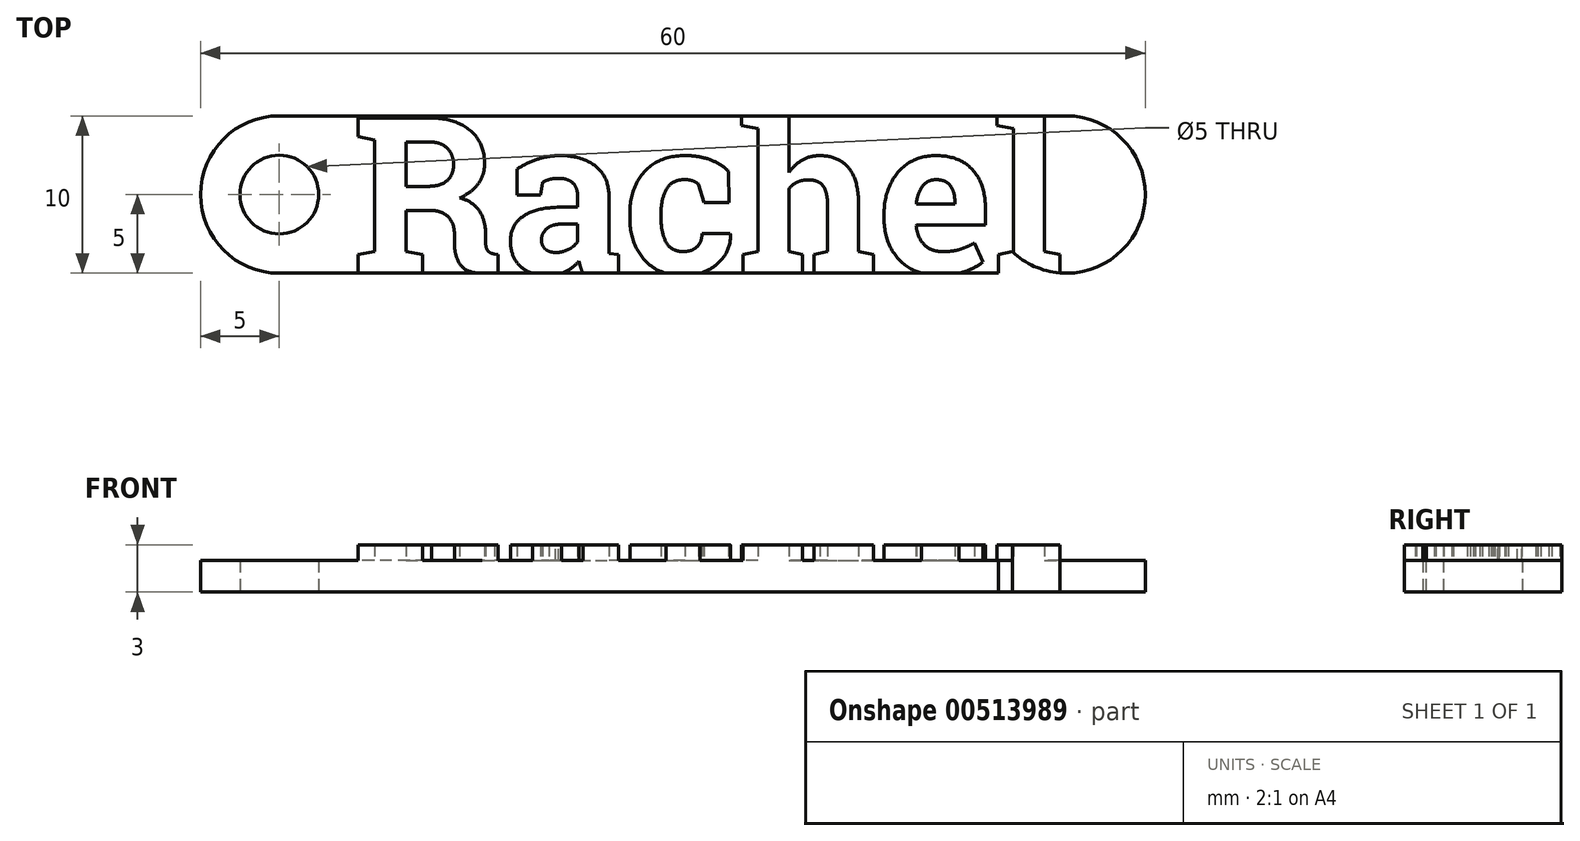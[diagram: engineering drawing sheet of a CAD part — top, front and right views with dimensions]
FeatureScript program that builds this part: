
annotation { "Feature Type Name" : "Feature", "Feature Type Description" : "" }
export const myFeature = defineFeature(function(context is Context, id is Id, definition is map)
    precondition{}
    {
        {
            var Q0;
            Q0=qCreatedBy(makeId("Top.planeOp"),FACE);
            var sketch = newSketch(context, id + "F0", { "sketchPlane" : qUnion([Q0])});
            skCircle(sketch, "E0", {"center": v(-30, 0) * mm, "radius": 2.5 * mm});
            skCircle(sketch, "E1", {"center": v(-30, 0) * mm, "radius": 5 * mm});
            skCircle(sketch, "E2", {"center": v(20, 0) * mm, "radius": 5 * mm});
            skLineSegment(sketch, "E3", {"start": v(-30, 5) * mm, "end": v(20, 5) * mm});
            skLineSegment(sketch, "E4", {"start": v(-30, -5) * mm, "end": v(20, -5) * mm});
            skText(sketch, "E5", { "text": "Rachel", "fontName": "RobotoSlab-Bold.ttf"});
            const initialGuessF0  = {"E5": [-0.02537, -0.005, 1, 0, 0.01]};
            skSetInitialGuess(sketch, initialGuessF0);
            skSolve(sketch);
        }
        {
            var Q0;
            {var subQ0=sQuery(id+"F0.wireOp",EDGE,"6bbc4e0a-0422-471a-a432-42bab2623723.sketch_text.stroke-9");Q0=makeQuery(id+"F0.imprint","IMPRINT",FACE,{"disambiguationData":[TD([[makeQuery(id+"F0.imprint","IMPRINT",EDGE,{"derivedFrom":subQ0}),1.0]])]});}
            var Q1;
            Q1=makeQuery(id+"F0.imprint","IMPRINT",FACE,{"disambiguationData":[TD([[makeQuery(id+"F0.imprint","IMPRINT",EDGE,{"derivedFrom":sQuery(id+"F0.wireOp",EDGE,"6bbc4e0a-0422-471a-a432-42bab2623723.sketch_text.stroke-0")}),1.0]])]});
            var Q2;
            Q2=makeQuery(id+"F0.imprint","IMPRINT",FACE,{"disambiguationData":[TD([[makeQuery(id+"F0.imprint","IMPRINT",EDGE,{"derivedFrom":sQuery(id+"F0.wireOp",EDGE,"6bbc4e0a-0422-471a-a432-42bab2623723.sketch_text.stroke-55")}),1.0]])]});
            var Q3;
            {var subQ5=sQuery(id+"F0.wireOp",EDGE,"6bbc4e0a-0422-471a-a432-42bab2623723.sketch_text.stroke-47");Q3=makeQuery(id+"F0.imprint","IMPRINT",FACE,{"disambiguationData":[TD([[makeQuery(id+"F0.imprint","IMPRINT",EDGE,{"derivedFrom":subQ5}),1.0]])]});}
            var Q4;
            {var subQ0=sQuery(id+"F0.wireOp",EDGE,"6bbc4e0a-0422-471a-a432-42bab2623723.sketch_text.stroke-71");Q4=makeQuery(id+"F0.imprint","IMPRINT",FACE,{"disambiguationData":[TD([[makeQuery(id+"F0.imprint","IMPRINT",EDGE,{"derivedFrom":subQ0}),1.0]])]});}
            var Q5;
            {var subQ0=sQuery(id+"F0.wireOp",EDGE,"E2");var subQ1=makeQuery(id+"F0.imprint","INTERSECT",VERTEX,{"derivedFrom":[subQ0,sQuery(id+"F0.wireOp",EDGE,"E3")]});Q5=makeQuery(id+"F0.imprint","IMPRINT",FACE,{"disambiguationData":[TD([[makeQuery(id+"F0.imprint","IMPRINT",EDGE,{"disambiguationData":[TD([[subQ1,-1.0]])],"derivedFrom":subQ0}),1.0]])]});}
            var Q6;
            Q6=makeQuery(id+"F0.imprint","IMPRINT",FACE,{"disambiguationData":[TD([[makeQuery(id+"F0.imprint","IMPRINT",EDGE,{"derivedFrom":sQuery(id+"F0.wireOp",EDGE,"E0")}),-1.0]])]});
            var Q7;
            Q7=makeQuery(id+"F0.imprint","IMPRINT",FACE,{"disambiguationData":[TD([[makeQuery(id+"F0.imprint","IMPRINT",EDGE,{"derivedFrom":sQuery(id+"F0.wireOp",EDGE,"6bbc4e0a-0422-471a-a432-42bab2623723.sketch_text.stroke-0")}),-1.0]])]});
            var Q8;
            Q8=makeQuery(id+"F0.imprint","IMPRINT",FACE,{"disambiguationData":[TD([[makeQuery(id+"F0.imprint","IMPRINT",EDGE,{"derivedFrom":sQuery(id+"F0.wireOp",EDGE,"6bbc4e0a-0422-471a-a432-42bab2623723.sketch_text.stroke-28")}),-1.0]])]});
            var Q9;
            {var subQ13=sQuery(id+"F0.wireOp",EDGE,"6bbc4e0a-0422-471a-a432-42bab2623723.sketch_text.stroke-47");Q9=makeQuery(id+"F0.imprint","IMPRINT",FACE,{"disambiguationData":[TD([[makeQuery(id+"F0.imprint","IMPRINT",EDGE,{"derivedFrom":subQ13}),-1.0]])]});}
            var Q10;
            Q10=makeQuery(id+"F0.imprint","IMPRINT",FACE,{"disambiguationData":[TD([[makeQuery(id+"F0.imprint","IMPRINT",EDGE,{"derivedFrom":sQuery(id+"F0.wireOp",EDGE,"6bbc4e0a-0422-471a-a432-42bab2623723.sketch_text.stroke-63")}),-1.0]])]});
            var Q11;
            {var subQ0=sQuery(id+"F0.wireOp",EDGE,"6bbc4e0a-0422-471a-a432-42bab2623723.sketch_text.stroke-70");var subQ1=sQuery(id+"F0.wireOp",EDGE,"E2");var subQ2=makeQuery(id+"F0.imprint","INTERSECT",VERTEX,{"disambiguationData":[OD(0.0)],"derivedFrom":[subQ1,subQ0]});Q11=makeQuery(id+"F0.imprint","IMPRINT",FACE,{"disambiguationData":[TD([[makeQuery(id+"F0.imprint","IMPRINT",EDGE,{"disambiguationData":[TD([[subQ2,-1.0]])],"derivedFrom":subQ1}),1.0]])]});}
            var Q12;
            {var subQ18=sQuery(id+"F0.wireOp",EDGE,"050f35f0-ba4d-4e93-975a-b973c0c4c371.sketch_text.stroke-12");Q12=makeQuery(id+"F0.imprint","IMPRINT",FACE,{"disambiguationData":[TD([[makeQuery(id+"F0.imprint","IMPRINT",EDGE,{"derivedFrom":subQ18}),1.0]])]});}
            var Q13;
            Q13=makeQuery(id+"F0.imprint","IMPRINT",FACE,{"disambiguationData":[TD([[makeQuery(id+"F0.imprint","IMPRINT",EDGE,{"derivedFrom":sQuery(id+"F0.wireOp",EDGE,"050f35f0-ba4d-4e93-975a-b973c0c4c371.sketch_text.stroke-0")}),1.0]])]});
            var Q14;
            Q14=makeQuery(id+"F0.imprint","IMPRINT",FACE,{"disambiguationData":[TD([[makeQuery(id+"F0.imprint","IMPRINT",EDGE,{"derivedFrom":sQuery(id+"F0.wireOp",EDGE,"050f35f0-ba4d-4e93-975a-b973c0c4c371.sketch_text.stroke-0")}),-1.0]])]});
            var Q15;
            Q15=makeQuery(id+"F0.imprint","IMPRINT",FACE,{"disambiguationData":[TD([[makeQuery(id+"F0.imprint","IMPRINT",EDGE,{"derivedFrom":sQuery(id+"F0.wireOp",EDGE,"050f35f0-ba4d-4e93-975a-b973c0c4c371.sketch_text.stroke-31")}),-1.0]])]});
            var Q16;
            {var subQ13=sQuery(id+"F0.wireOp",EDGE,"050f35f0-ba4d-4e93-975a-b973c0c4c371.sketch_text.stroke-57");Q16=makeQuery(id+"F0.imprint","IMPRINT",FACE,{"disambiguationData":[TD([[makeQuery(id+"F0.imprint","IMPRINT",EDGE,{"derivedFrom":subQ13}),-1.0]])]});}
            var Q17;
            Q17=makeQuery(id+"F0.imprint","IMPRINT",FACE,{"disambiguationData":[TD([[makeQuery(id+"F0.imprint","IMPRINT",EDGE,{"derivedFrom":sQuery(id+"F0.wireOp",EDGE,"050f35f0-ba4d-4e93-975a-b973c0c4c371.sketch_text.stroke-67")}),1.0]])]});
            var Q18;
            {var subQ7=sQuery(id+"F0.wireOp",EDGE,"050f35f0-ba4d-4e93-975a-b973c0c4c371.sketch_text.stroke-57");Q18=makeQuery(id+"F0.imprint","IMPRINT",FACE,{"disambiguationData":[TD([[makeQuery(id+"F0.imprint","IMPRINT",EDGE,{"derivedFrom":subQ7}),1.0]])]});}
            var Q19;
            {var subQ5=sQuery(id+"F0.wireOp",EDGE,"050f35f0-ba4d-4e93-975a-b973c0c4c371.sketch_text.stroke-83");Q19=makeQuery(id+"F0.imprint","IMPRINT",FACE,{"disambiguationData":[TD([[makeQuery(id+"F0.imprint","IMPRINT",EDGE,{"derivedFrom":subQ5}),-1.0]])]});}
            var Q20;
            {var subQ0=sQuery(id+"F0.wireOp",EDGE,"050f35f0-ba4d-4e93-975a-b973c0c4c371.sketch_text.stroke-77");var subQ1=sQuery(id+"F0.wireOp",EDGE,"E2");var subQ2=makeQuery(id+"F0.imprint","INTERSECT",VERTEX,{"derivedFrom":[subQ1,subQ0]});Q20=makeQuery(id+"F0.imprint","IMPRINT",FACE,{"disambiguationData":[TD([[makeQuery(id+"F0.imprint","IMPRINT",EDGE,{"disambiguationData":[TD([[subQ2,-1.0]])],"derivedFrom":subQ1}),1.0]])]});}
            var Q21;
            {var subQ0=sQuery(id+"F0.wireOp",EDGE,"050f35f0-ba4d-4e93-975a-b973c0c4c371.sketch_text.stroke-78");var subQ1=sQuery(id+"F0.wireOp",EDGE,"E2");var subQ2=makeQuery(id+"F0.imprint","INTERSECT",VERTEX,{"derivedFrom":[subQ1,subQ0]});Q21=makeQuery(id+"F0.imprint","IMPRINT",FACE,{"disambiguationData":[TD([[makeQuery(id+"F0.imprint","IMPRINT",EDGE,{"disambiguationData":[TD([[subQ2,-1.0]])],"derivedFrom":subQ1}),-1.0]])]});}
            var Q22;
            {var subQ0=sQuery(id+"F0.wireOp",EDGE,"050f35f0-ba4d-4e93-975a-b973c0c4c371.sketch_text.stroke-80");Q22=makeQuery(id+"F0.imprint","IMPRINT",FACE,{"disambiguationData":[TD([[makeQuery(id+"F0.imprint","IMPRINT",EDGE,{"derivedFrom":subQ0}),-1.0]])]});}
            var Q23;
            {var subQ0=sQuery(id+"F0.wireOp",EDGE,"E4");var subQ1=sQuery(id+"F0.wireOp",EDGE,"E2");var subQ2=makeQuery(id+"F0.imprint","INTERSECT",VERTEX,{"derivedFrom":[subQ1,subQ0]});Q23=makeQuery(id+"F0.imprint","IMPRINT",FACE,{"disambiguationData":[TD([[makeQuery(id+"F0.imprint","IMPRINT",EDGE,{"disambiguationData":[TD([[subQ2,1.0]])],"derivedFrom":subQ1}),-1.0]])]});}
            var Q24;
            Q24=makeQuery(id+"F0.imprint","IMPRINT",FACE,{"disambiguationData":[TD([[makeQuery(id+"F0.imprint","IMPRINT",EDGE,{"derivedFrom":sQuery(id+"F0.wireOp",EDGE,"E5.sketch_text.stroke-0")}),1.0]])]});
            var Q25;
            Q25=makeQuery(id+"F0.imprint","IMPRINT",FACE,{"disambiguationData":[TD([[makeQuery(id+"F0.imprint","IMPRINT",EDGE,{"derivedFrom":sQuery(id+"F0.wireOp",EDGE,"E5.sketch_text.stroke-29")}),1.0]])]});
            var Q26;
            Q26=makeQuery(id+"F0.imprint","IMPRINT",FACE,{"disambiguationData":[TD([[makeQuery(id+"F0.imprint","IMPRINT",EDGE,{"derivedFrom":sQuery(id+"F0.wireOp",EDGE,"E5.sketch_text.stroke-63")}),1.0]])]});
            var Q27;
            {var subQ5=sQuery(id+"F0.wireOp",EDGE,"E5.sketch_text.stroke-100");Q27=makeQuery(id+"F0.imprint","IMPRINT",FACE,{"disambiguationData":[TD([[makeQuery(id+"F0.imprint","IMPRINT",EDGE,{"derivedFrom":subQ5}),1.0]])]});}
            var Q28;
            {var subQ6=sQuery(id+"F0.wireOp",EDGE,"E5.sketch_text.stroke-121");Q28=makeQuery(id+"F0.imprint","IMPRINT",FACE,{"disambiguationData":[TD([[makeQuery(id+"F0.imprint","IMPRINT",EDGE,{"derivedFrom":subQ6}),-1.0]])]});}
            var Q29;
            {var subQ0=sQuery(id+"F0.wireOp",EDGE,"E5.sketch_text.stroke-147");Q29=makeQuery(id+"F0.imprint","IMPRINT",FACE,{"disambiguationData":[TD([[makeQuery(id+"F0.imprint","IMPRINT",EDGE,{"derivedFrom":subQ0}),-1.0]])]});}
            var Q30;
            {var subQ0=sQuery(id+"F0.wireOp",EDGE,"E5.sketch_text.stroke-152");var subQ1=sQuery(id+"F0.wireOp",EDGE,"E2");var subQ2=makeQuery(id+"F0.imprint","INTERSECT",VERTEX,{"derivedFrom":[subQ1,subQ0]});Q30=makeQuery(id+"F0.imprint","IMPRINT",FACE,{"disambiguationData":[TD([[makeQuery(id+"F0.imprint","IMPRINT",EDGE,{"disambiguationData":[TD([[subQ2,-1.0]])],"derivedFrom":subQ1}),1.0]])]});}
            var Q31;
            Q31=makeQuery(id+"F0.imprint","IMPRINT",FACE,{"disambiguationData":[TD([[makeQuery(id+"F0.imprint","IMPRINT",EDGE,{"derivedFrom":sQuery(id+"F0.wireOp",EDGE,"E5.sketch_text.stroke-137")}),1.0]])]});
            var Q32;
            {var subQ0=sQuery(id+"F0.wireOp",EDGE,"E5.sketch_text.stroke-108");Q32=makeQuery(id+"F0.imprint","IMPRINT",FACE,{"disambiguationData":[TD([[makeQuery(id+"F0.imprint","IMPRINT",EDGE,{"derivedFrom":subQ0}),1.0]])]});}
            var Q33;
            Q33=makeQuery(id+"F0.imprint","IMPRINT",FACE,{"disambiguationData":[TD([[makeQuery(id+"F0.imprint","IMPRINT",EDGE,{"derivedFrom":sQuery(id+"F0.wireOp",EDGE,"E5.sketch_text.stroke-36")}),-1.0]])]});
            var Q34;
            {var subQ0=sQuery(id+"F0.wireOp",EDGE,"E5.sketch_text.stroke-12");Q34=makeQuery(id+"F0.imprint","IMPRINT",FACE,{"disambiguationData":[TD([[makeQuery(id+"F0.imprint","IMPRINT",EDGE,{"derivedFrom":subQ0}),1.0]])]});}
            var Q35;
            Q35=makeQuery(id+"F0.imprint","IMPRINT",FACE,{"disambiguationData":[TD([[makeQuery(id+"F0.imprint","IMPRINT",EDGE,{"derivedFrom":sQuery(id+"F0.wireOp",EDGE,"E5.sketch_text.stroke-0")}),-1.0]])]});
            var Q36;
            Q36=makeQuery(id+"F0.imprint","IMPRINT",FACE,{"disambiguationData":[TD([[makeQuery(id+"F0.imprint","IMPRINT",EDGE,{"derivedFrom":sQuery(id+"F0.wireOp",EDGE,"E5.sketch_text.stroke-71")}),-1.0]])]});
            var Q37;
            Q37=makeQuery(id+"F0.imprint","IMPRINT",FACE,{"disambiguationData":[TD([[makeQuery(id+"F0.imprint","IMPRINT",EDGE,{"derivedFrom":sQuery(id+"F0.wireOp",EDGE,"E5.sketch_text.stroke-94")}),-1.0]])]});
            var Q38;
            {var subQ1=sQuery(id+"F0.wireOp",EDGE,"E5.sketch_text.stroke-149");Q38=makeQuery(id+"F0.imprint","IMPRINT",FACE,{"disambiguationData":[TD([[makeQuery(id+"F0.imprint","IMPRINT",EDGE,{"derivedFrom":subQ1}),-1.0]])]});}
            var Q39;
            {var subQ5=sQuery(id+"F0.wireOp",EDGE,"E5.sketch_text.stroke-153");Q39=makeQuery(id+"F0.imprint","IMPRINT",FACE,{"disambiguationData":[TD([[makeQuery(id+"F0.imprint","IMPRINT",EDGE,{"derivedFrom":subQ5}),-1.0]])]});}
            var Q40;
            {var subQ1=sQuery(id+"F0.wireOp",EDGE,"E5.sketch_text.stroke-36");Q40=makeQuery(id+"F0.imprint","IMPRINT",FACE,{"disambiguationData":[TD([[makeQuery(id+"F0.imprint","IMPRINT",EDGE,{"derivedFrom":subQ1}),1.0]])]});}
            extrude(context, id + "F1", {"entities" : qUnion([Q0, Q1, Q2, Q3, Q4, Q5, Q6, Q7, Q8, Q9, Q10, Q11, Q12, Q13, Q14, Q15, Q16, Q17, Q18, Q19, Q20, Q21, Q22, Q23, Q24, Q25, Q26, Q27, Q28, Q29, Q30, Q31, Q32, Q33, Q34, Q35, Q36, Q37, Q38, Q39, Q40]), "depth" : 2 * mm, "offsetDistance" : 25 * mm});
        }
        {
            var Q0;
            Q0=makeQuery(id+"F0.imprint","IMPRINT",FACE,{"disambiguationData":[TD([[makeQuery(id+"F0.imprint","IMPRINT",EDGE,{"derivedFrom":sQuery(id+"F0.wireOp",EDGE,"E5.sketch_text.stroke-0")}),-1.0]])]});
            var Q1;
            Q1=makeQuery(id+"F0.imprint","IMPRINT",FACE,{"disambiguationData":[TD([[makeQuery(id+"F0.imprint","IMPRINT",EDGE,{"derivedFrom":sQuery(id+"F0.wireOp",EDGE,"E5.sketch_text.stroke-36")}),-1.0]])]});
            var Q2;
            Q2=makeQuery(id+"F0.imprint","IMPRINT",FACE,{"disambiguationData":[TD([[makeQuery(id+"F0.imprint","IMPRINT",EDGE,{"derivedFrom":sQuery(id+"F0.wireOp",EDGE,"E5.sketch_text.stroke-71")}),-1.0]])]});
            var Q3;
            Q3=makeQuery(id+"F0.imprint","IMPRINT",FACE,{"disambiguationData":[TD([[makeQuery(id+"F0.imprint","IMPRINT",EDGE,{"derivedFrom":sQuery(id+"F0.wireOp",EDGE,"E5.sketch_text.stroke-94")}),-1.0]])]});
            var Q4;
            {var subQ6=sQuery(id+"F0.wireOp",EDGE,"E5.sketch_text.stroke-121");Q4=makeQuery(id+"F0.imprint","IMPRINT",FACE,{"disambiguationData":[TD([[makeQuery(id+"F0.imprint","IMPRINT",EDGE,{"derivedFrom":subQ6}),-1.0]])]});}
            var Q5;
            {var subQ0=sQuery(id+"F0.wireOp",EDGE,"E5.sketch_text.stroke-147");Q5=makeQuery(id+"F0.imprint","IMPRINT",FACE,{"disambiguationData":[TD([[makeQuery(id+"F0.imprint","IMPRINT",EDGE,{"derivedFrom":subQ0}),-1.0]])]});}
            var Q6;
            {var subQ5=sQuery(id+"F0.wireOp",EDGE,"E5.sketch_text.stroke-153");Q6=makeQuery(id+"F0.imprint","IMPRINT",FACE,{"disambiguationData":[TD([[makeQuery(id+"F0.imprint","IMPRINT",EDGE,{"derivedFrom":subQ5}),-1.0]])]});}
            var Q7;
            {var subQ1=sQuery(id+"F0.wireOp",EDGE,"E5.sketch_text.stroke-149");Q7=makeQuery(id+"F0.imprint","IMPRINT",FACE,{"disambiguationData":[TD([[makeQuery(id+"F0.imprint","IMPRINT",EDGE,{"derivedFrom":subQ1}),-1.0]])]});}
            extrude(context, id + "F2", {"entities" : qUnion([Q0, Q1, Q2, Q3, Q4, Q5, Q6, Q7]), "operationType" : NewBodyOperationType.ADD, "depth" : 3 * mm, "offsetDistance" : 25 * mm});
        }
    });
